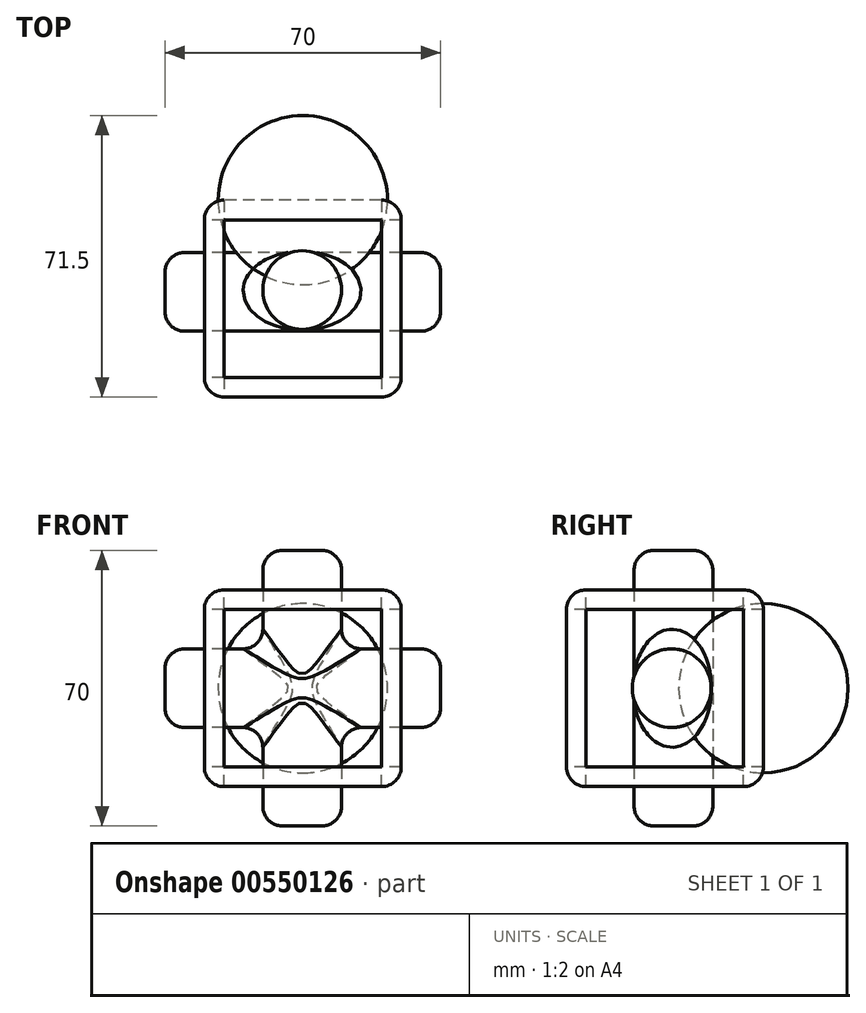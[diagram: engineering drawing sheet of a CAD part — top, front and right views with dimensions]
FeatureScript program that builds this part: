
annotation { "Feature Type Name" : "Feature", "Feature Type Description" : "" }
export const myFeature = defineFeature(function(context is Context, id is Id, definition is map)
    precondition{}
    {
        {
            var Q0;
            Q0=qCreatedBy(makeId("Front.planeOp"),FACE);
            var sketch = newSketch(context, id + "F0", { "sketchPlane" : qUnion([Q0])});
            skLineSegment(sketch, "E0.bottom", {"start": v(25, 25) * mm, "end": v(-25, 25) * mm});
            skLineSegment(sketch, "E0.top", {"start": v(25, -25) * mm, "end": v(-25, -25) * mm});
            skLineSegment(sketch, "E0.left", {"start": v(25, 25) * mm, "end": v(25, -25) * mm});
            skLineSegment(sketch, "E0.right", {"start": v(-25, 25) * mm, "end": v(-25, -25) * mm});
            skPoint(sketch, "E0.middle", {"position": v(0, 0) * mm});
            skSolve(sketch);
        }
        {
            var Q0;
            Q0 = qSketchRegion(id + "F0", true);
            extrude(context, id + "F1", {"entities" : qUnion([Q0]), "depth" : 50 * mm, "offsetDistance" : 25 * mm});
        }
        {
            var Q0;
            Q0=makeQuery(id+"F1.opExtrude","CAP_EDGE",EDGE,{"disambiguationData":[OSD([sQuery(id+"F0.wireOp",EDGE,"E0.bottom")])],"isStart":false});
            var Q1;
            Q1=makeQuery(id+"F1.opExtrude","CAP_EDGE",EDGE,{"disambiguationData":[OSD([sQuery(id+"F0.wireOp",EDGE,"E0.right")])],"isStart":false});
            var Q2;
            Q2=makeQuery(id+"F1.opExtrude","CAP_EDGE",EDGE,{"disambiguationData":[OSD([sQuery(id+"F0.wireOp",EDGE,"E0.top")])],"isStart":false});
            var Q3;
            Q3=makeQuery(id+"F1.opExtrude","CAP_EDGE",EDGE,{"disambiguationData":[OSD([sQuery(id+"F0.wireOp",EDGE,"E0.left")])],"isStart":false});
            var Q4;
            Q4=makeQuery(id+"F1.opExtrude","SWEPT_FACE",FACE,{"disambiguationData":[OSD([sQuery(id+"F0.wireOp",EDGE,"E0.top")])]});
            var Q5;
            Q5=makeQuery(id+"F1.opExtrude","SWEPT_EDGE",EDGE,{"disambiguationData":[OSD([sQuery(id+"F0.wireOp",EDGE,"E0.top"),sQuery(id+"F0.wireOp",EDGE,"E0.right")])]});
            var Q6;
            Q6=makeQuery(id+"F1.opExtrude","SWEPT_EDGE",EDGE,{"disambiguationData":[OSD([sQuery(id+"F0.wireOp",EDGE,"E0.top"),sQuery(id+"F0.wireOp",EDGE,"E0.left")])]});
            var Q7;
            Q7=makeQuery(id+"F1.opExtrude","SWEPT_EDGE",EDGE,{"disambiguationData":[OSD([sQuery(id+"F0.wireOp",EDGE,"E0.bottom"),sQuery(id+"F0.wireOp",EDGE,"E0.left")])]});
            var Q8;
            Q8=makeQuery(id+"F1.opExtrude","SWEPT_EDGE",EDGE,{"disambiguationData":[OSD([sQuery(id+"F0.wireOp",EDGE,"E0.bottom"),sQuery(id+"F0.wireOp",EDGE,"E0.right")])]});
            var Q9;
            Q9=makeQuery(id+"F1.opExtrude","SWEPT_FACE",FACE,{"disambiguationData":[OSD([sQuery(id+"F0.wireOp",EDGE,"E0.bottom")])]});
            var Q10;
            Q10=makeQuery(id+"F1.opExtrude","CAP_EDGE",EDGE,{"disambiguationData":[OSD([sQuery(id+"F0.wireOp",EDGE,"E0.right")])],"isStart":true});
            var Q11;
            Q11=makeQuery(id+"F1.opExtrude","CAP_FACE",FACE,{"disambiguationData":[OSD([sQuery(id+"F0.wireOp",EDGE,"E0.bottom"),sQuery(id+"F0.wireOp",EDGE,"E0.top"),sQuery(id+"F0.wireOp",EDGE,"E0.left"),sQuery(id+"F0.wireOp",EDGE,"E0.right")])],"isStart":true});
            fillet(context, id + "F2", {"entities" : qUnion([Q0, Q1, Q2, Q3, Q4, Q5, Q6, Q7, Q8, Q9, Q10, Q11]), "radius" : 5 * mm, "tangentPropagation" : true, "allowEdgeOverflow" : false});
        }
        {
            var Q0;
            Q0=makeQuery(id+"F1.opExtrude","CAP_FACE",FACE,{"disambiguationData":[OSD([sQuery(id+"F0.wireOp",EDGE,"E0.bottom"),sQuery(id+"F0.wireOp",EDGE,"E0.top"),sQuery(id+"F0.wireOp",EDGE,"E0.left"),sQuery(id+"F0.wireOp",EDGE,"E0.right")])],"isStart":false});
            extrude(context, id + "F3", {"entities" : qUnion([Q0]), "operationType" : NewBodyOperationType.REMOVE, "oppositeDirection" : true, "depth" : 60 * mm, "offsetDistance" : 25 * mm});
        }
        {
            var Q0;
            Q0=makeQuery(id+"F1.opExtrude","SWEPT_FACE",FACE,{"disambiguationData":[OSD([sQuery(id+"F0.wireOp",EDGE,"E0.right")])]});
            extrude(context, id + "F4", {"entities" : qUnion([Q0]), "operationType" : NewBodyOperationType.REMOVE, "oppositeDirection" : true, "depth" : 60 * mm, "offsetDistance" : 25 * mm});
        }
        {
            var Q0;
            Q0=makeQuery(id+"F1.opExtrude","SWEPT_FACE",FACE,{"disambiguationData":[OSD([sQuery(id+"F0.wireOp",EDGE,"E0.bottom")])]});
            extrude(context, id + "F5", {"entities" : qUnion([Q0]), "operationType" : NewBodyOperationType.REMOVE, "oppositeDirection" : true, "depth" : 50 * mm, "offsetDistance" : 25 * mm});
        }
        {
            var Q0;
            Q0=qCreatedBy(makeId("Top.planeOp"),FACE);
            var sketch = newSketch(context, id + "F6", { "sketchPlane" : qUnion([Q0])});
            skCircle(sketch, "E1", {"center": v(-0.16, -22.85) * mm, "radius": 10 * mm});
            skSolve(sketch);
        }
        {
            var Q0;
            Q0=makeQuery(id+"F6.imprint","IMPRINT",FACE,{"disambiguationData":[TD([[makeQuery(id+"F6.imprint","IMPRINT",EDGE,{"derivedFrom":sQuery(id+"F6.wireOp",EDGE,"E1")}),1.0]])]});
            extrude(context, id + "F7", {"entities" : qUnion([Q0]), "endBound" : BoundingType.SYMMETRIC, "depth" : 70 * mm, "offsetDistance" : 25 * mm});
        }
        {
            var Q0;
            Q0=qCreatedBy(makeId("Right.planeOp"),FACE);
            var sketch = newSketch(context, id + "F8", { "sketchPlane" : qUnion([Q0])});
            skCircle(sketch, "E2", {"center": v(-23.3, 0) * mm, "radius": 10 * mm});
            skSolve(sketch);
        }
        {
            var Q0;
            Q0 = qSketchRegion(id + "F8", true);
            extrude(context, id + "F9", {"entities" : qUnion([Q0]), "operationType" : NewBodyOperationType.ADD, "endBound" : BoundingType.SYMMETRIC, "depth" : 70 * mm, "offsetDistance" : 25 * mm});
        }
        {
            var Q0;
            Q0=makeQuery(id+"F7.opExtrude","SWEPT_FACE",FACE,{"disambiguationData":[OSD([sQuery(id+"F6.wireOp",EDGE,"E1")])]});
            var Q1;
            Q1=makeQuery(id+"F9.opExtrude","SWEPT_FACE",FACE,{"disambiguationData":[OSD([sQuery(id+"F8.wireOp",EDGE,"E2")])]});
            fillet(context, id + "F10", {"entities" : qUnion([Q0, Q1]), "radius" : 5 * mm, "tangentPropagation" : true, "allowEdgeOverflow" : false});
        }
        {
            var Q0;
            Q0=qCreatedBy(makeId("Front.planeOp"),FACE);
            var sketch = newSketch(context, id + "F11", { "sketchPlane" : qUnion([Q0])});
            skCircle(sketch, "E3", {"center": v(0, 0) * mm, "radius": 21.5 * mm});
            skLineSegment(sketch, "E4", {"start": v(0, 21.5) * mm, "end": v(0, -21.5) * mm, "construction": true});
            skLineSegment(sketch, "E5", {"start": v(0, 25.82) * mm, "end": v(0, -26.8) * mm});
            skSolve(sketch);
        }
        {
            var Q0;
            {var subQ0=sQuery(id+"F11.wireOp",EDGE,"E5");var subQ1=sQuery(id+"F11.wireOp",EDGE,"E3");var subQ2=makeQuery(id+"F11.imprint","INTERSECT",VERTEX,{"disambiguationData":[OD(0.0)],"derivedFrom":[subQ1,subQ0]});Q0=makeQuery(id+"F11.imprint","IMPRINT",FACE,{"disambiguationData":[TD([[makeQuery(id+"F11.imprint","IMPRINT",EDGE,{"disambiguationData":[TD([[subQ2,-1.0]])],"derivedFrom":subQ1}),1.0]])]});}
            var Q1;
            Q1=sQuery(id+"F11.wireOp",EDGE,"E5");
            revolve(context, id + "F12", {"entities" : qUnion([Q0]), "axis" : qUnion([Q1]), "revolveType" : RevolveType.FULL});
        }
    });
